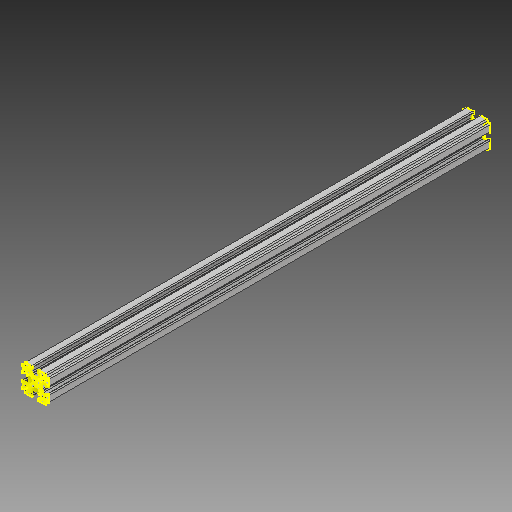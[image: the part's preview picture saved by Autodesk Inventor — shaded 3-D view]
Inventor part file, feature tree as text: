
AUTODESK INVENTOR PART (.ipt)
format: ipt  version: 2018.3 (Build 223284000, 284)  size: 742,912 bytes
history: native  units: mm
features: sketch x5, projected_geometry x5, extrude x3, plane x1, fillet x1
ambient origin geometry x8: Origin, YZ Plane, XZ Plane, XY Plane, X Axis, Y Axis, Z Axis, Center Point
bodies: Solid1 (feature_tree)
feature tree (15):
  sketch  "Sketch1"  dims[d0=10.0mm d1=0.0mm d2=165.1mm d3=0.0mm]
  plane  "Work Plane1"
  extrude  "Extrusion1"  Depth=165.1mm TaperAngle=0.0deg
  sketch  "Sketch2"  dims[d4=29.4mm d5=0.0mm]
  extrude  "Extrusion2"  [1 undecoded]
  extrude  "Extrusion3"  [1 undecoded]
  sketch  "Sketch5"
  projected_geometry  "Projected Loop1"
  projected_geometry  "Projected Loop2"
  sketch  "Sketch3"
  projected_geometry  "Projected Loop3"
  sketch  "Sketch4"
  projected_geometry  "Projected Loop4"
  projected_geometry  "Projected Loop5"
  fillet  "Fillet6"  [1 undecoded]
note: 3 required parameter values undecoded (feature->parameter linkage not recoverable at this tier; creation-order binding heuristic only, values carry confidence <= 0.55)
